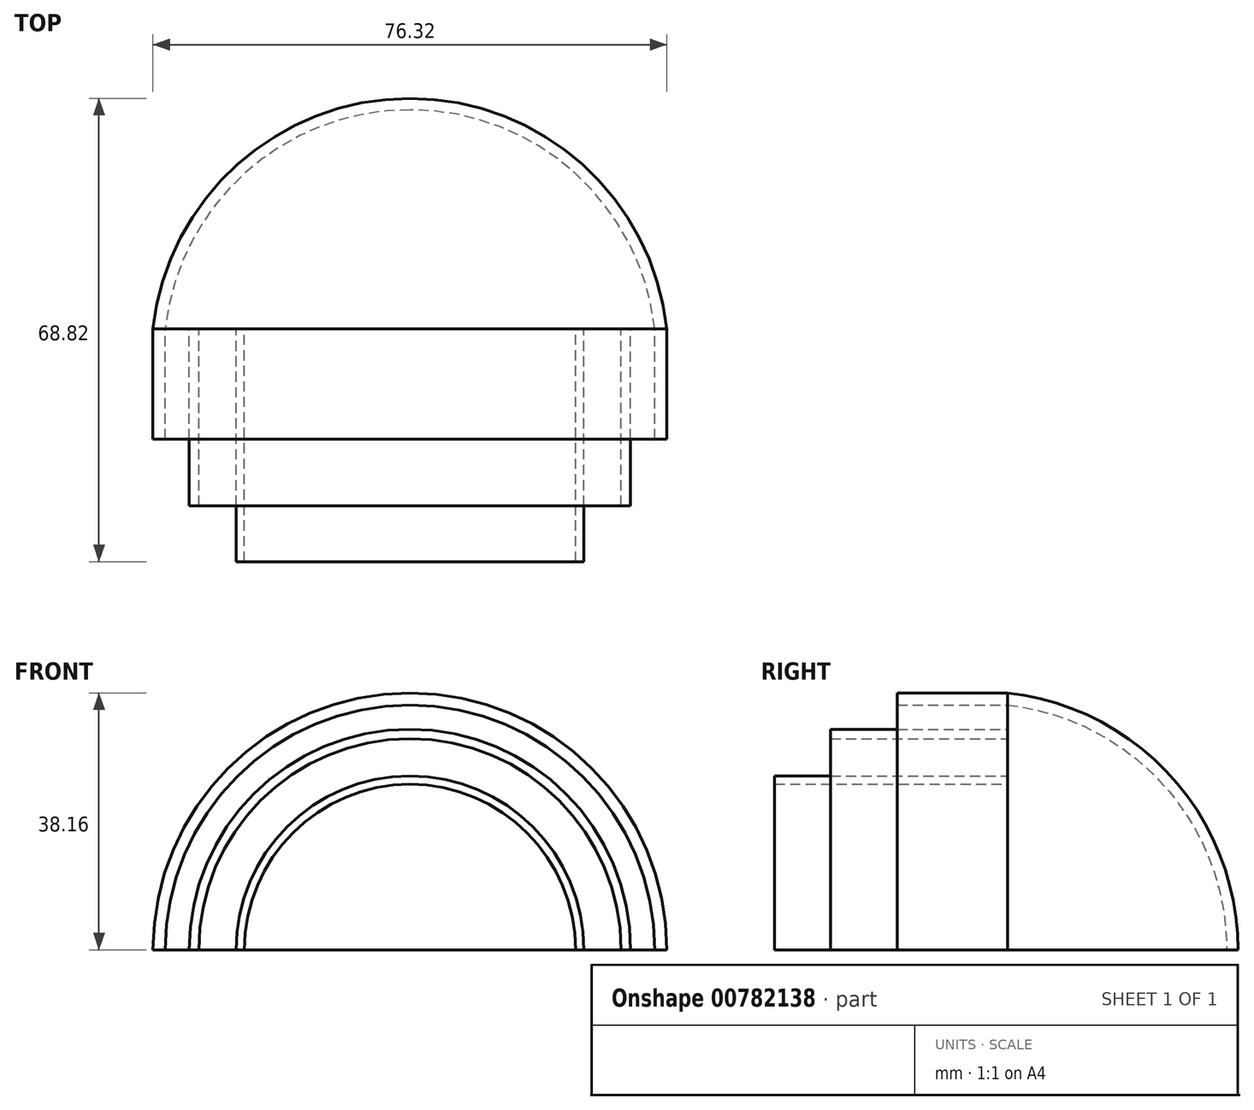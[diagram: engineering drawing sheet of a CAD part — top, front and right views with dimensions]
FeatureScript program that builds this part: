
annotation { "Feature Type Name" : "Feature", "Feature Type Description" : "" }
export const myFeature = defineFeature(function(context is Context, id is Id, definition is map)
    precondition{}
    {
        {
            var Q0;
            Q0=qCreatedBy(makeId("Front.planeOp"),FACE);
            var sketch = newSketch(context, id + "F0", { "sketchPlane" : qUnion([Q0])});
            skArc(sketch, "E0", {"start": v(24.59, 0) * mm, "mid": v(0, 24.59) * mm, "end": v(-24.59, 0) * mm});
            skArc(sketch, "E1", {"start": v(25.83, 0) * mm, "mid": v(0, 25.83) * mm, "end": v(-25.83, 0) * mm});
            skArc(sketch, "E2", {"start": v(31.35, 0) * mm, "mid": v(0, 31.35) * mm, "end": v(-31.35, 0) * mm});
            skArc(sketch, "E3", {"start": v(32.77, 0) * mm, "mid": v(0, 32.77) * mm, "end": v(-32.77, 0) * mm});
            skArc(sketch, "E4", {"start": v(36.35, 0) * mm, "mid": v(0, 36.35) * mm, "end": v(-36.35, 0) * mm});
            skArc(sketch, "E5", {"start": v(38.16, 0) * mm, "mid": v(0, 38.16) * mm, "end": v(-38.16, 0) * mm});
            skLineSegment(sketch, "E6", {"start": v(-38.16, 0) * mm, "end": v(38.16, 0) * mm});
            skSolve(sketch);
        }
        {
            var Q0;
            {var subQ0=sQuery(id+"F0.wireOp",EDGE,"E0");Q0=makeQuery(id+"F0.imprint","IMPRINT",FACE,{"disambiguationData":[TD([[makeQuery(id+"F0.imprint","IMPRINT",EDGE,{"derivedFrom":subQ0}),-1.0]])]});}
            extrude(context, id + "F1", {"entities" : qUnion([Q0]), "depth" : 34.6 * mm, "offsetDistance" : 25 * mm});
        }
        {
            var Q0;
            {var subQ0=sQuery(id+"F0.wireOp",EDGE,"E2");Q0=makeQuery(id+"F0.imprint","IMPRINT",FACE,{"disambiguationData":[TD([[makeQuery(id+"F0.imprint","IMPRINT",EDGE,{"derivedFrom":subQ0}),-1.0]])]});}
            extrude(context, id + "F2", {"entities" : qUnion([Q0]), "depth" : 26.3 * mm, "offsetDistance" : 25 * mm});
        }
        {
            var Q0;
            {var subQ0=sQuery(id+"F0.wireOp",EDGE,"E4");Q0=makeQuery(id+"F0.imprint","IMPRINT",FACE,{"disambiguationData":[TD([[makeQuery(id+"F0.imprint","IMPRINT",EDGE,{"derivedFrom":subQ0}),-1.0]])]});}
            extrude(context, id + "F3", {"entities" : qUnion([Q0]), "depth" : 16.4 * mm, "offsetDistance" : 25 * mm});
        }
        {
            var Q0;
            Q0=qCreatedBy(makeId("Top.planeOp"),FACE);
            var sketch = newSketch(context, id + "F4", { "sketchPlane" : qUnion([Q0])});
            skArc(sketch, "E7", {"start": v(0, 34.22) * mm, "mid": v(-25.61, 24.4) * mm, "end": v(-38.16, 0) * mm});
            skLineSegment(sketch, "E8", {"start": v(0, 0) * mm, "end": v(0, 34.22) * mm});
            skPoint(sketch, "E9.orphan", {"position": v(38.26, 0) * mm});
            skLineSegment(sketch, "E10", {"start": v(-38.16, 0) * mm, "end": v(-36.36, 0) * mm});
            skArc(sketch, "E11", {"start": v(0, 32.52) * mm, "mid": v(-24.4, 23.22) * mm, "end": v(-36.36, 0) * mm});
            skPoint(sketch, "E12.orphan", {"position": v(36.3, 0) * mm});
            skLineSegment(sketch, "E13", {"start": v(0, 34.22) * mm, "end": v(0, 32.52) * mm});
            skSolve(sketch);
        }
        {
            var Q0;
            Q0=makeQuery(id+"F4.imprint","IMPRINT",FACE,{"disambiguationData":[TD([[makeQuery(id+"F4.imprint","IMPRINT",EDGE,{"derivedFrom":sQuery(id+"F4.wireOp",EDGE,"E7")}),1.0]])]});
            var Q1;
            Q1=sQuery(id+"F4.wireOp",EDGE,"E8");
            revolve(context, id + "F5", {"operationType" : NewBodyOperationType.ADD, "surfaceOperationType" : NewSurfaceOperationType.NEW, "entities" : qUnion([Q0]), "axis" : qUnion([Q1]), "revolveType" : RevolveType.ONE_DIRECTION, "angle" : 180 * degree});
        }
    });
